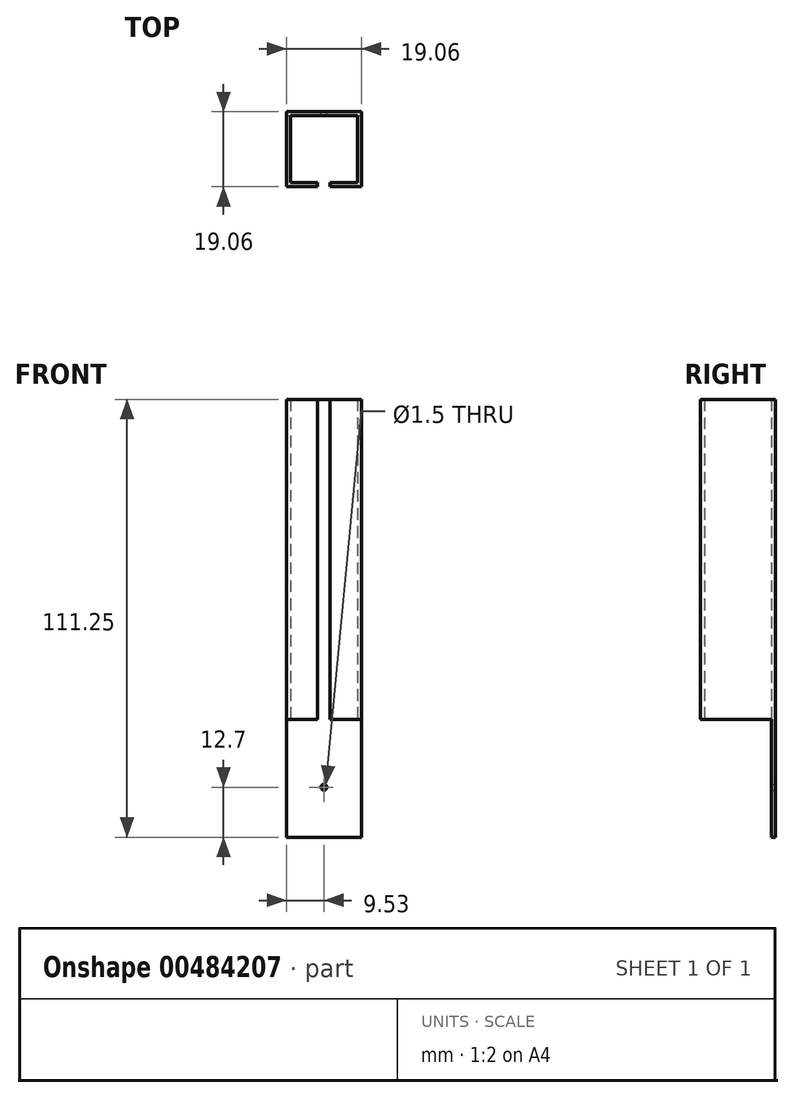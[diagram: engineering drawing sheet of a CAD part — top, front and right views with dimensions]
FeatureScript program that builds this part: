
annotation { "Feature Type Name" : "Feature", "Feature Type Description" : "" }
export const myFeature = defineFeature(function(context is Context, id is Id, definition is map)
    precondition{}
    {
        {
            var Q0;
            Q0=qCreatedBy(makeId("Top.planeOp"),FACE);
            var sketch = newSketch(context, id + "F0", { "sketchPlane" : qUnion([Q0])});
            skLineSegment(sketch, "E0.bottom", {"start": v(-9.52, 9.53) * mm, "end": v(9.53, 9.53) * mm});
            skLineSegment(sketch, "E0.top", {"start": v(-9.53, -9.52) * mm, "end": v(9.52, -9.52) * mm});
            skLineSegment(sketch, "E0.left", {"start": v(-9.52, 9.53) * mm, "end": v(-9.53, -9.52) * mm});
            skLineSegment(sketch, "E0.right", {"start": v(9.53, 9.53) * mm, "end": v(9.52, -9.52) * mm});
            skPoint(sketch, "E0.middle", {"position": v(0, 0) * mm});
            skLineSegment(sketch, "E1.0", {"start": v(-8.5, 8.5) * mm, "end": v(8.5, 8.5) * mm});
            skLineSegment(sketch, "E1.1", {"start": v(-8.5, 8.5) * mm, "end": v(-8.5, -8.5) * mm});
            skLineSegment(sketch, "E1.2", {"start": v(-8.5, -8.5) * mm, "end": v(8.5, -8.5) * mm});
            skLineSegment(sketch, "E1.3", {"start": v(8.5, 8.5) * mm, "end": v(8.5, -8.5) * mm});
            skSolve(sketch);
        }
        {
            var Q0;
            Q0=makeQuery(id+"F0.imprint","IMPRINT",FACE,{"disambiguationData":[TD([[makeQuery(id+"F0.imprint","IMPRINT",EDGE,{"derivedFrom":sQuery(id+"F0.wireOp",EDGE,"E0.bottom")}),-1.0]])]});
            extrude(context, id + "F1", {"entities" : qUnion([Q0]), "depth" : 111.25 * mm});
        }
        {
            var Q0;
            Q0=makeQuery(id+"F1.opExtrude","SWEPT_FACE",FACE,{"disambiguationData":[OSD([sQuery(id+"F0.wireOp",EDGE,"E0.top")])]});
            var sketch = newSketch(context, id + "F2", { "sketchPlane" : qUnion([Q0])});
            skLineSegment(sketch, "E2.bottom", {"start": v(-1.59, 111.25) * mm, "end": v(1.59, 111.25) * mm});
            skLineSegment(sketch, "E2.top", {"start": v(-1.59, 0) * mm, "end": v(1.59, 0) * mm});
            skLineSegment(sketch, "E2.left", {"start": v(-1.59, 111.25) * mm, "end": v(-1.59, 0) * mm});
            skLineSegment(sketch, "E2.right", {"start": v(1.59, 111.25) * mm, "end": v(1.59, 0) * mm});
            skPoint(sketch, "E2.middle", {"position": v(0, 55.63) * mm});
            skSolve(sketch);
        }
        {
            var Q0;
            Q0 = qSketchRegion(id + "F2", true);
            var Q1;
            Q1=makeQuery(id+"F1.opExtrude","SWEPT_FACE",FACE,{"disambiguationData":[OSD([sQuery(id+"F0.wireOp",EDGE,"E1.2")])]});
            extrude(context, id + "F3", {"entities" : qUnion([Q0]), "operationType" : NewBodyOperationType.REMOVE, "endBound" : BoundingType.UP_TO_SURFACE, "oppositeDirection" : true, "endBoundEntityFace" : qUnion([Q1]), "depth" : 25.4 * mm});
        }
        {
            var Q0;
            Q0=makeQuery(id+"F1.opExtrude","SWEPT_FACE",FACE,{"disambiguationData":[OSD([sQuery(id+"F0.wireOp",EDGE,"E0.right")])]});
            var sketch = newSketch(context, id + "F4", { "sketchPlane" : qUnion([Q0])});
            skLineSegment(sketch, "E3.bottom", {"start": v(-9.52, 0) * mm, "end": v(8.5, 0) * mm});
            skLineSegment(sketch, "E3.top", {"start": v(-9.52, 29.97) * mm, "end": v(8.5, 29.97) * mm});
            skLineSegment(sketch, "E3.left", {"start": v(-9.52, 0) * mm, "end": v(-9.52, 29.97) * mm});
            skLineSegment(sketch, "E3.right", {"start": v(8.5, 0) * mm, "end": v(8.5, 29.97) * mm});
            skSolve(sketch);
        }
        {
            var Q0;
            Q0 = qSketchRegion(id + "F4", true);
            extrude(context, id + "F5", {"entities" : qUnion([Q0]), "operationType" : NewBodyOperationType.REMOVE, "endBound" : BoundingType.THROUGH_ALL, "oppositeDirection" : true, "depth" : 25.4 * mm});
        }
        {
            var Q0;
            Q0=makeQuery(id+"F1.opExtrude","SWEPT_FACE",FACE,{"disambiguationData":[OSD([sQuery(id+"F0.wireOp",EDGE,"E0.bottom")])]});
            var sketch = newSketch(context, id + "F6", { "sketchPlane" : qUnion([Q0])});
            skCircle(sketch, "E4", {"center": v(0, 12.7) * mm, "radius": 0.75 * mm});
            skSolve(sketch);
        }
        {
            var Q0;
            Q0 = qSketchRegion(id + "F6", true);
            extrude(context, id + "F7", {"entities" : qUnion([Q0]), "operationType" : NewBodyOperationType.REMOVE, "endBound" : BoundingType.THROUGH_ALL, "oppositeDirection" : true, "depth" : 25.4 * mm});
        }
    });
